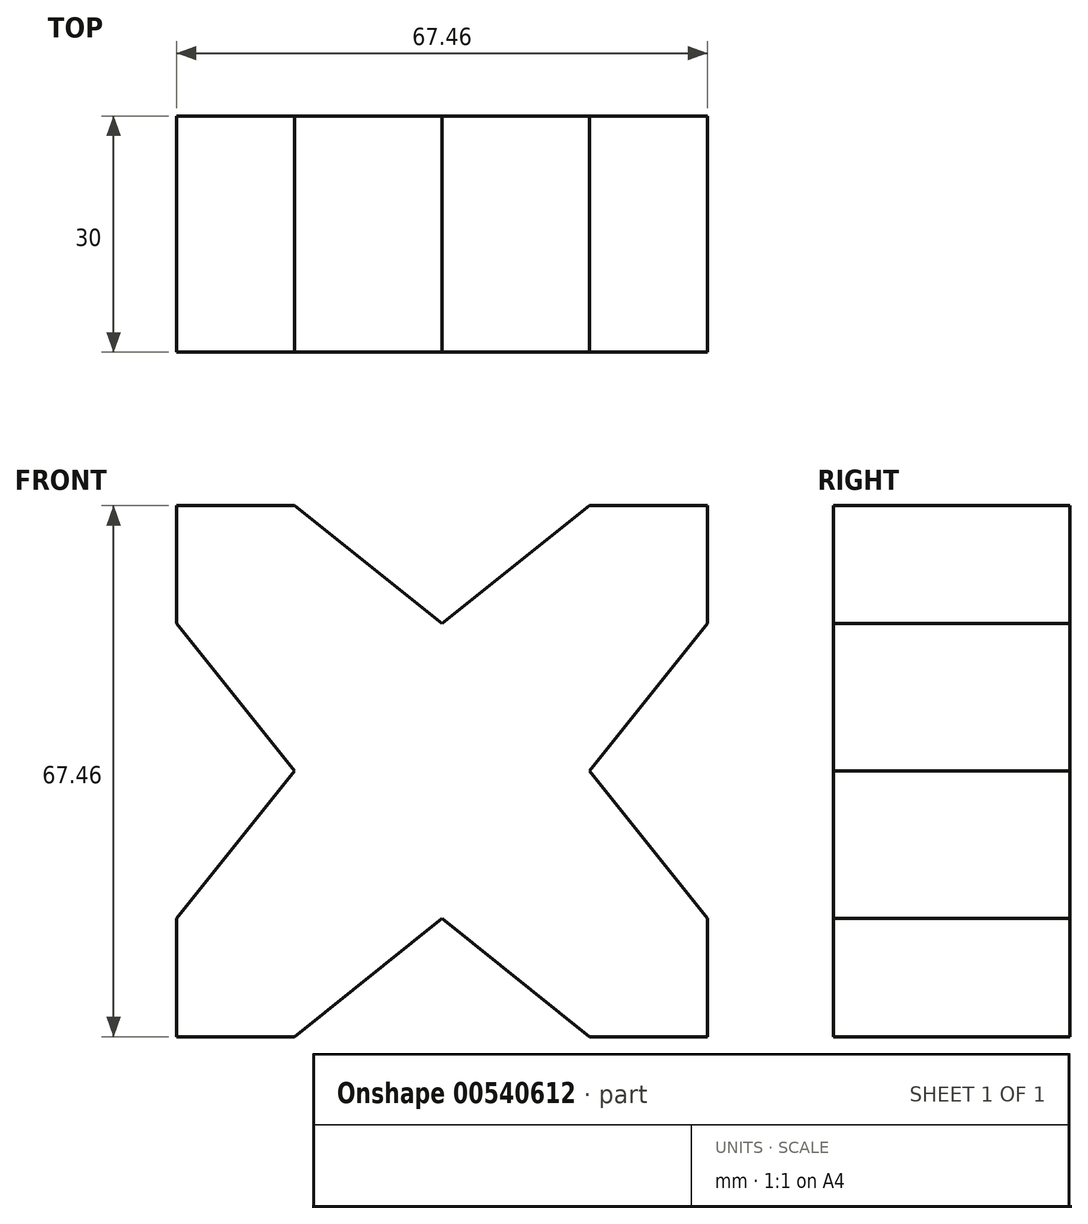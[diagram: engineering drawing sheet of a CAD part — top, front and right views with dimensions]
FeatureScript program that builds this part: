
annotation { "Feature Type Name" : "Feature", "Feature Type Description" : "" }
export const myFeature = defineFeature(function(context is Context, id is Id, definition is map)
    precondition{}
    {
        {
            var Q0;
            Q0=qCreatedBy(makeId("Front.planeOp"),FACE);
            var sketch = newSketch(context, id + "F0", { "sketchPlane" : qUnion([Q0])});
            skLineSegment(sketch, "E0", {"start": v(-33.73, 33.73) * mm, "end": v(-33.73, 18.73) * mm});
            skLineSegment(sketch, "E1", {"start": v(-33.73, 18.73) * mm, "end": v(-18.73, 0) * mm});
            skLineSegment(sketch, "E2", {"start": v(-18.73, 0) * mm, "end": v(-33.73, -18.73) * mm});
            skLineSegment(sketch, "E3", {"start": v(-33.73, -18.73) * mm, "end": v(-33.73, -33.73) * mm});
            skLineSegment(sketch, "E4", {"start": v(-33.73, -33.73) * mm, "end": v(-18.73, -33.73) * mm});
            skLineSegment(sketch, "E5", {"start": v(-18.73, -33.73) * mm, "end": v(0, -18.73) * mm});
            skLineSegment(sketch, "E6", {"start": v(0, -18.73) * mm, "end": v(18.73, -33.73) * mm});
            skLineSegment(sketch, "E7", {"start": v(18.73, -33.73) * mm, "end": v(33.73, -33.73) * mm});
            skLineSegment(sketch, "E8", {"start": v(33.73, -33.73) * mm, "end": v(33.73, -18.73) * mm});
            skLineSegment(sketch, "E9", {"start": v(33.73, -18.73) * mm, "end": v(18.73, 0) * mm});
            skLineSegment(sketch, "E10", {"start": v(18.73, 0) * mm, "end": v(33.73, 18.73) * mm});
            skLineSegment(sketch, "E11", {"start": v(33.73, 18.73) * mm, "end": v(33.73, 33.73) * mm});
            skLineSegment(sketch, "E12", {"start": v(18.73, 33.73) * mm, "end": v(33.73, 33.73) * mm});
            skLineSegment(sketch, "E13", {"start": v(18.73, 33.73) * mm, "end": v(0, 18.73) * mm});
            skLineSegment(sketch, "E14", {"start": v(0, 18.73) * mm, "end": v(-18.73, 33.73) * mm});
            skLineSegment(sketch, "E15", {"start": v(-18.73, 33.73) * mm, "end": v(-33.73, 33.73) * mm});
            skLineSegment(sketch, "E16", {"start": v(-18.73, -33.73) * mm, "end": v(18.73, -33.73) * mm, "construction": true});
            skSolve(sketch);
        }
        {
            var Q0;
            Q0 = qSketchRegion(id + "F0", true);
            extrude(context, id + "F1", {"entities" : qUnion([Q0]), "depth" : 30 * mm, "offsetDistance" : 25 * mm});
        }
    });
